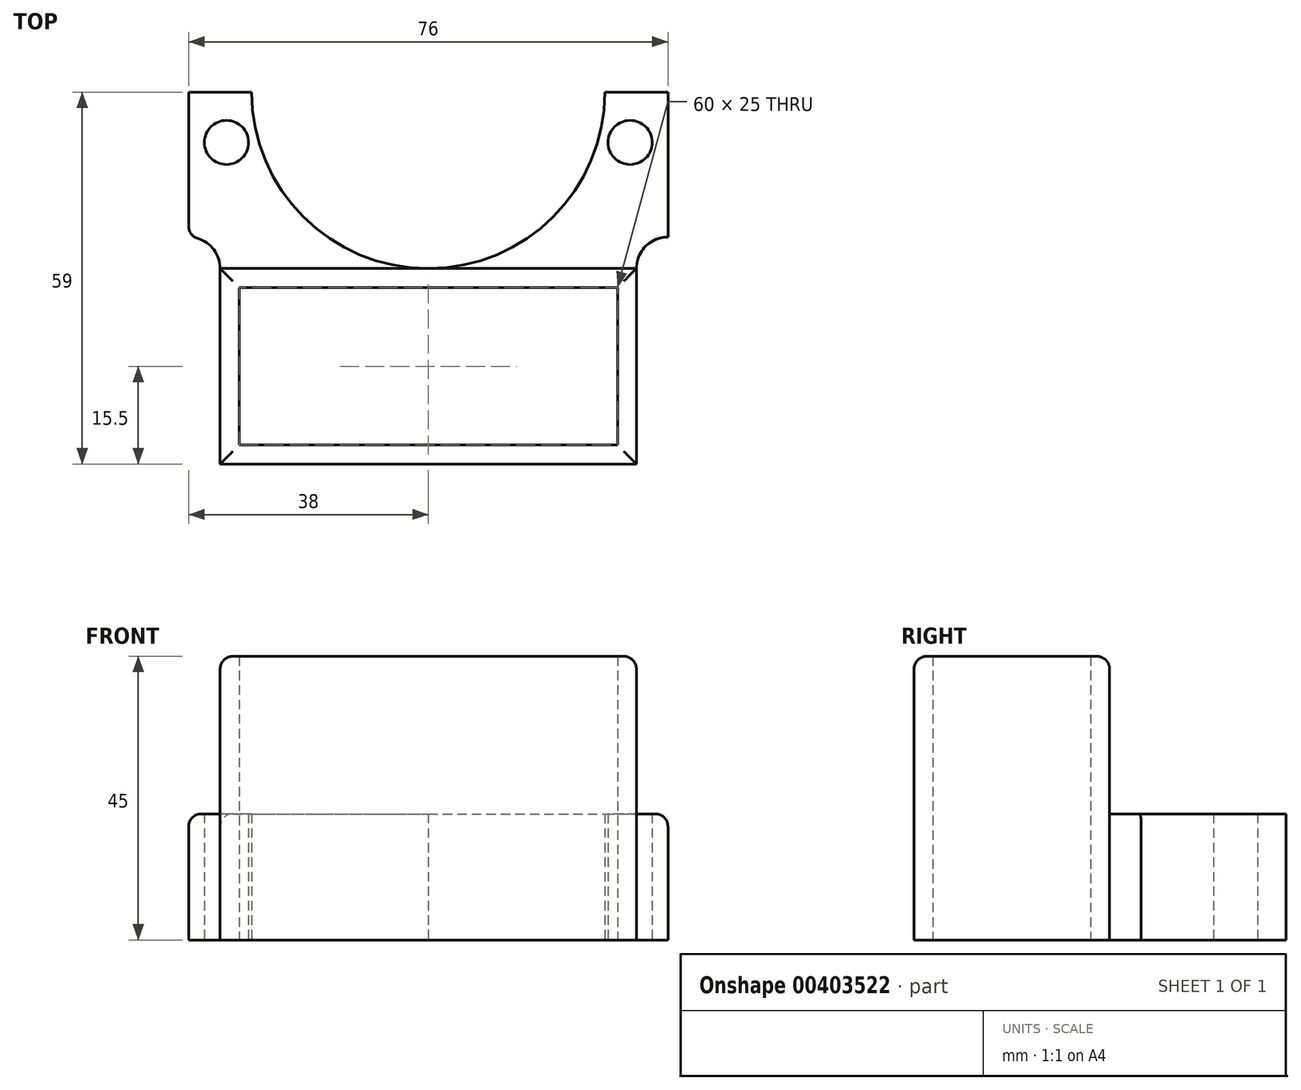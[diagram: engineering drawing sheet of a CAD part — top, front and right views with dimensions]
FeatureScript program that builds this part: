
annotation { "Feature Type Name" : "Feature", "Feature Type Description" : "" }
export const myFeature = defineFeature(function(context is Context, id is Id, definition is map)
    precondition{}
    {
        {
            var Q0;
            Q0=qCreatedBy(makeId("Top.planeOp"),FACE);
            var sketch = newSketch(context, id + "F0", { "sketchPlane" : qUnion([Q0])});
            skLineSegment(sketch, "E0.bottom", {"start": v(30, -12.5) * mm, "end": v(-30, -12.5) * mm});
            skLineSegment(sketch, "E0.top", {"start": v(30, 12.5) * mm, "end": v(-30, 12.5) * mm});
            skLineSegment(sketch, "E0.left", {"start": v(30, -12.5) * mm, "end": v(30, 12.5) * mm});
            skLineSegment(sketch, "E0.right", {"start": v(-30, -12.5) * mm, "end": v(-30, 12.5) * mm});
            skPoint(sketch, "E0.middle", {"position": v(0, 0) * mm});
            skLineSegment(sketch, "E1.bottom", {"start": v(33, -15.5) * mm, "end": v(-33, -15.5) * mm});
            skLineSegment(sketch, "E1.left", {"start": v(33, -15.5) * mm, "end": v(33, 15.5) * mm});
            skLineSegment(sketch, "E1.right", {"start": v(-33, -15.5) * mm, "end": v(-33, 15.5) * mm});
            skPoint(sketch, "E2", {"position": v(0, 43.5) * mm});
            skPoint(sketch, "E3", {"position": v(-28, 43.5) * mm});
            skPoint(sketch, "E4", {"position": v(28, 43.5) * mm});
            skArc(sketch, "E5", {"start": v(-28, 43.5) * mm, "mid": v(0, 15.5) * mm, "end": v(28, 43.5) * mm});
            skLineSegment(sketch, "E6.bottom", {"start": v(-28, 43.5) * mm, "end": v(-25, 43.5) * mm});
            skArc(sketch, "E7", {"start": v(25, 43.5) * mm, "mid": v(0, 18.5) * mm, "end": v(-25, 43.5) * mm});
            skLineSegment(sketch, "E8.bottom", {"start": v(28, 43.5) * mm, "end": v(38, 43.5) * mm});
            skLineSegment(sketch, "E9.bottom", {"start": v(-28, 43.5) * mm, "end": v(-38, 43.5) * mm});
            skLineSegment(sketch, "E9.right", {"start": v(-38, 43.5) * mm, "end": v(-38, 20.5) * mm});
            skPoint(sketch, "E10", {"position": v(-32, 35.5) * mm});
            skPoint(sketch, "E11", {"position": v(32, 35.5) * mm});
            skCircle(sketch, "E12", {"center": v(-32, 35.5) * mm, "radius": 3.5 * mm});
            skCircle(sketch, "E13", {"center": v(32, 35.5) * mm, "radius": 3.5 * mm});
            skLineSegment(sketch, "E14", {"start": v(-38, 43.5) * mm, "end": v(-25, 43.5) * mm});
            skLineSegment(sketch, "E15", {"start": v(25, 43.5) * mm, "end": v(38, 43.5) * mm});
            skLineSegment(sketch, "E16", {"start": v(38, 43.5) * mm, "end": v(38, 20.5) * mm});
            skLineSegment(sketch, "E17.trimOffspring", {"start": v(25, 43.5) * mm, "end": v(28, 43.5) * mm});
            skLineSegment(sketch, "E18", {"start": v(-33, 15.5) * mm, "end": v(33, 15.5) * mm});
            skPoint(sketch, "E19", {"position": v(-38, 20.5) * mm});
            skPoint(sketch, "E20", {"position": v(38, 20.5) * mm});
            skArc(sketch, "E21", {"start": v(-33, 15.5) * mm, "mid": v(-34.46, 19.04) * mm, "end": v(-38, 20.5) * mm});
            skArc(sketch, "E22", {"start": v(38, 20.5) * mm, "mid": v(34.46, 19.04) * mm, "end": v(33, 15.5) * mm});
            skSolve(sketch);
        }
        {
            var Q0;
            Q0=makeQuery(id+"F0.imprint","IMPRINT",FACE,{"disambiguationData":[TD([[makeQuery(id+"F0.imprint","IMPRINT",EDGE,{"derivedFrom":sQuery(id+"F0.wireOp",EDGE,"E0.bottom")}),1.0]])]});
            extrude(context, id + "F1", {"entities" : qUnion([Q0]), "depth" : 45 * mm});
        }
        {
            var Q0;
            Q0=makeQuery(id+"F0.imprint","IMPRINT",FACE,{"disambiguationData":[TD([[makeQuery(id+"F0.imprint","IMPRINT",EDGE,{"derivedFrom":sQuery(id+"F0.wireOp",EDGE,"E13")}),-1.0]])]});
            var Q1;
            {var subQ3=sQuery(id+"F0.wireOp",EDGE,"E7");Q1=makeQuery(id+"F0.imprint","IMPRINT",FACE,{"disambiguationData":[TD([[makeQuery(id+"F0.imprint","IMPRINT",EDGE,{"derivedFrom":subQ3}),1.0]])]});}
            var Q2;
            {var subQ3=sQuery(id+"F0.wireOp",EDGE,"E9.right");Q2=makeQuery(id+"F0.imprint","IMPRINT",FACE,{"disambiguationData":[TD([[makeQuery(id+"F0.imprint","IMPRINT",EDGE,{"derivedFrom":subQ3}),1.0]])]});}
            extrude(context, id + "F2", {"entities" : qUnion([Q0, Q1, Q2]), "depth" : 20 * mm});
        }
        {
            var Q0;
            Q0=makeQuery(id+"F2.opExtrude","CAP_EDGE",EDGE,{"disambiguationData":[OSD([sQuery(id+"F0.wireOp",EDGE,"E16")])],"isStart":false});
            var Q1;
            Q1=makeQuery(id+"F2.opExtrude","CAP_EDGE",EDGE,{"disambiguationData":[OSD([sQuery(id+"F0.wireOp",EDGE,"E9.right")])],"isStart":false});
            var Q2;
            Q2=makeQuery(id+"F1.opExtrude","CAP_EDGE",EDGE,{"disambiguationData":[OSD([sQuery(id+"F0.wireOp",EDGE,"E1.top"),sQuery(id+"F0.wireOp",EDGE,"deb6854c-db62-4b70-b2c0-efcdc1d693f5.trimOffspring"),sQuery(id+"F0.wireOp",EDGE,"E18")])],"isStart":false});
            var Q3;
            Q3=makeQuery(id+"F1.opExtrude","CAP_EDGE",EDGE,{"disambiguationData":[OSD([sQuery(id+"F0.wireOp",EDGE,"E1.left")])],"isStart":false});
            var Q4;
            Q4=makeQuery(id+"F1.opExtrude","CAP_EDGE",EDGE,{"disambiguationData":[OSD([sQuery(id+"F0.wireOp",EDGE,"E1.bottom")])],"isStart":false});
            var Q5;
            Q5=makeQuery(id+"F1.opExtrude","CAP_EDGE",EDGE,{"disambiguationData":[OSD([sQuery(id+"F0.wireOp",EDGE,"E1.right")])],"isStart":false});
            fillet(context, id + "F3", {"entities" : qUnion([Q0, Q1, Q2, Q3, Q4, Q5]), "radius" : 2 * mm, "tangentPropagation" : true, "allowEdgeOverflow" : false});
        }
        {
            var Q0;
            Q0=makeQuery(id+"F2.opExtrude","SWEPT_EDGE",EDGE,{"disambiguationData":[OSD([sQuery(id+"F0.wireOp",EDGE,"E9.right"),sQuery(id+"F0.wireOp",EDGE,"E21")])]});
            fillet(context, id + "F4", {"entities" : qUnion([Q0]), "radius" : 2 * mm, "tangentPropagation" : true, "allowEdgeOverflow" : false});
        }
    });
